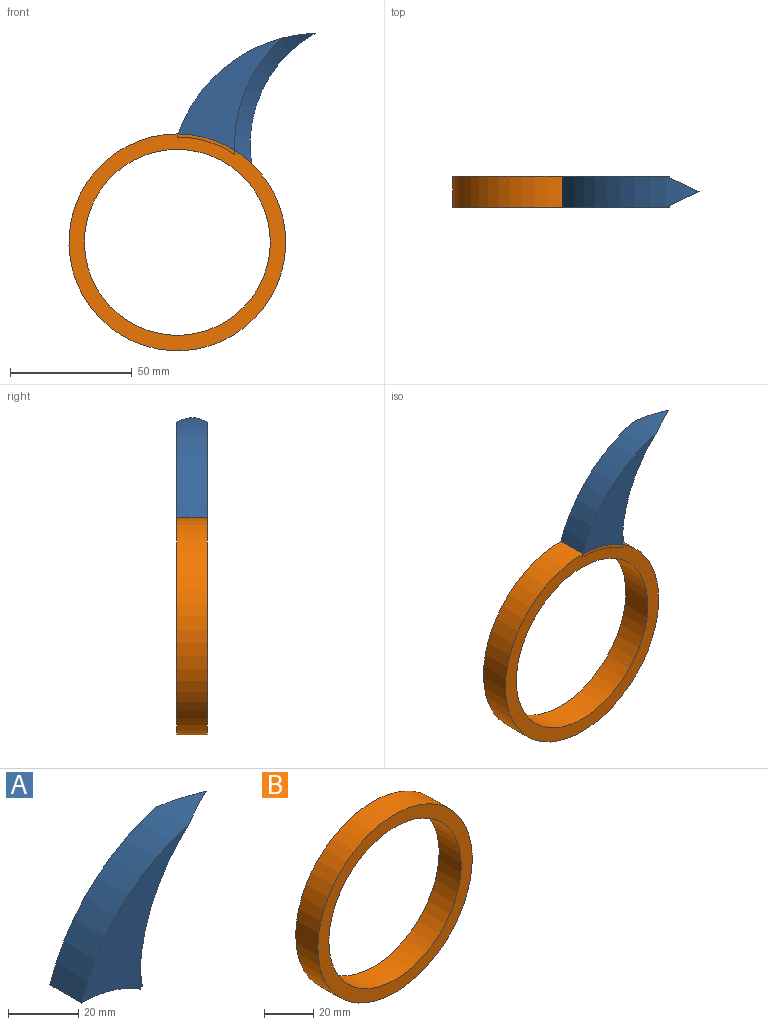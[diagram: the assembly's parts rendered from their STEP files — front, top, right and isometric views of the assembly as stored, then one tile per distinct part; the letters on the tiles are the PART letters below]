
ASSEMBLY  parts=2 mates=1
PART A: 6 faces, bbox 56.6x12.7x62.1 mm
  f0: cylinder r=61.44mm len=56.56mm, axis (0,1,0), area 870.2mm2, adj f1,f2,f3,f4,f5
  f1: cylinder r=43.14mm len=30.86mm, axis (0,1,0), area 373.9mm2, adj f0,f2,f3,f4,f5
  f2: plane 47.57x43.01mm, normal (0,-1,0), area 699.2mm2, adj f0,f1,f4
  f3: plane 47.57x43.01mm, normal (0,1,0), area 699.2mm2, adj f0,f1,f5
  f4: cone r=52.2mm half-angle=45deg, axis (0,-1,0), area 529.7mm2, adj f0,f1,f2,f5
  f5: cone r=58.55mm half-angle=45deg, axis (0,1,0), area 529.7mm2, adj f0,f1,f3,f4
PART B: 4 faces, bbox 88.9x12.7x88.9 mm
  f0: cylinder r=44.45mm len=88.9mm, axis (0,1,0), area 3547mm2, adj f1,f2
  f1: plane 88.9x88.9mm, normal (0,-1,0), area 1646.8mm2, adj f0,f3
  f2: plane 88.9x88.9mm, normal (0,1,0), area 1646.8mm2, adj f0,f3
  f3: cylinder r=38.1mm len=76.2mm, axis (0,-1,0), area 3040.2mm2, adj f1,f2
PLACE A t=(-202.08,-81.09,-106.31)mm
PLACE B rot(axis=(1,0,0),180deg) t=(-201.97,-93.79,-104.46)mm
MATE planar B.f0 <-> A.f1  axis (0,1,0) through (-201.97,-81.09,-104.46)mm
